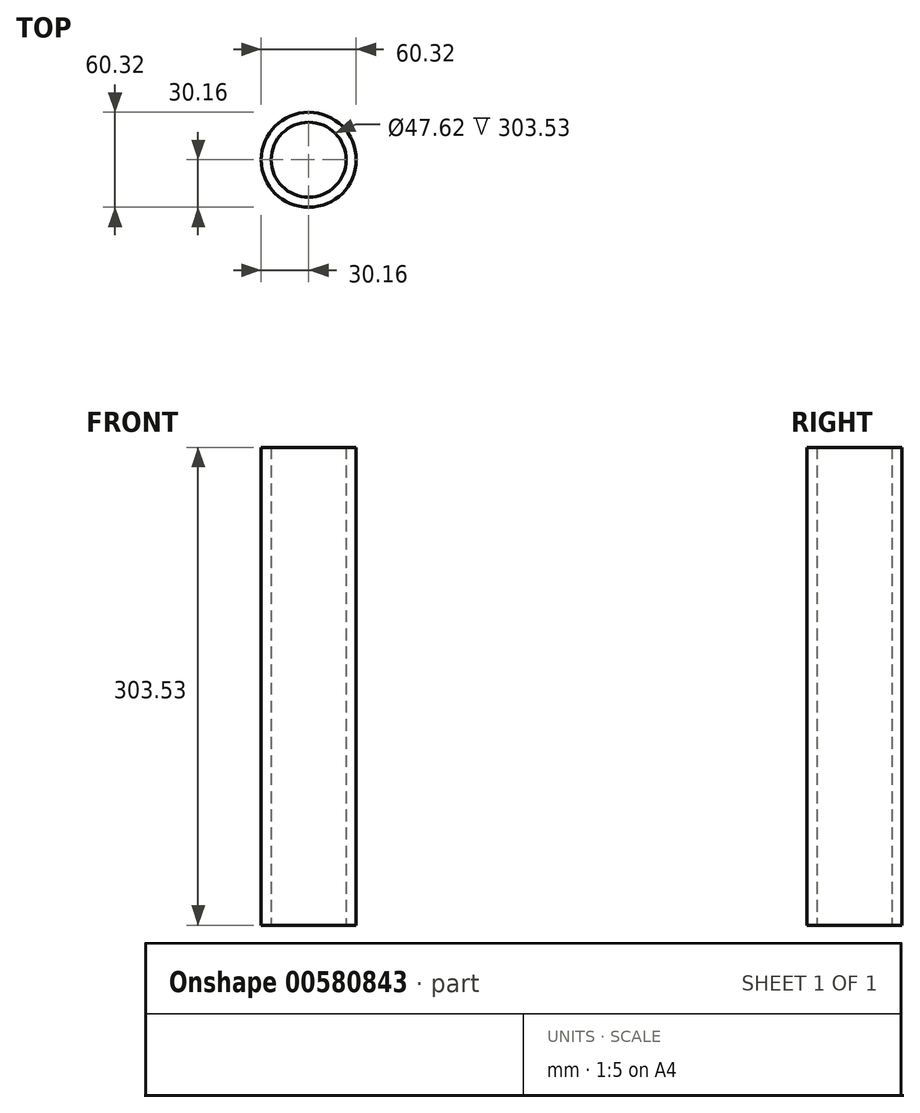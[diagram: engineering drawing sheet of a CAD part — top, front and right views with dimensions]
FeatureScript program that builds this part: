
annotation { "Feature Type Name" : "Feature", "Feature Type Description" : "" }
export const myFeature = defineFeature(function(context is Context, id is Id, definition is map)
    precondition{}
    {
        {
            var Q0;
            Q0=qCreatedBy(makeId("Top.planeOp"),FACE);
            var sketch = newSketch(context, id + "F0", { "sketchPlane" : qUnion([Q0])});
            skCircle(sketch, "E0", {"center": v(0, 0) * mm, "radius": 30.16 * mm});
            skCircle(sketch, "E1", {"center": v(0, 0) * mm, "radius": 23.81 * mm});
            skSolve(sketch);
        }
        {
            var Q0;
            Q0 = qSketchRegion(id + "F0", true);
            extrude(context, id + "F1", {"entities" : qUnion([Q0]), "depth" : 303.53 * mm, "offsetDistance" : 25.4 * mm});
        }
    });
